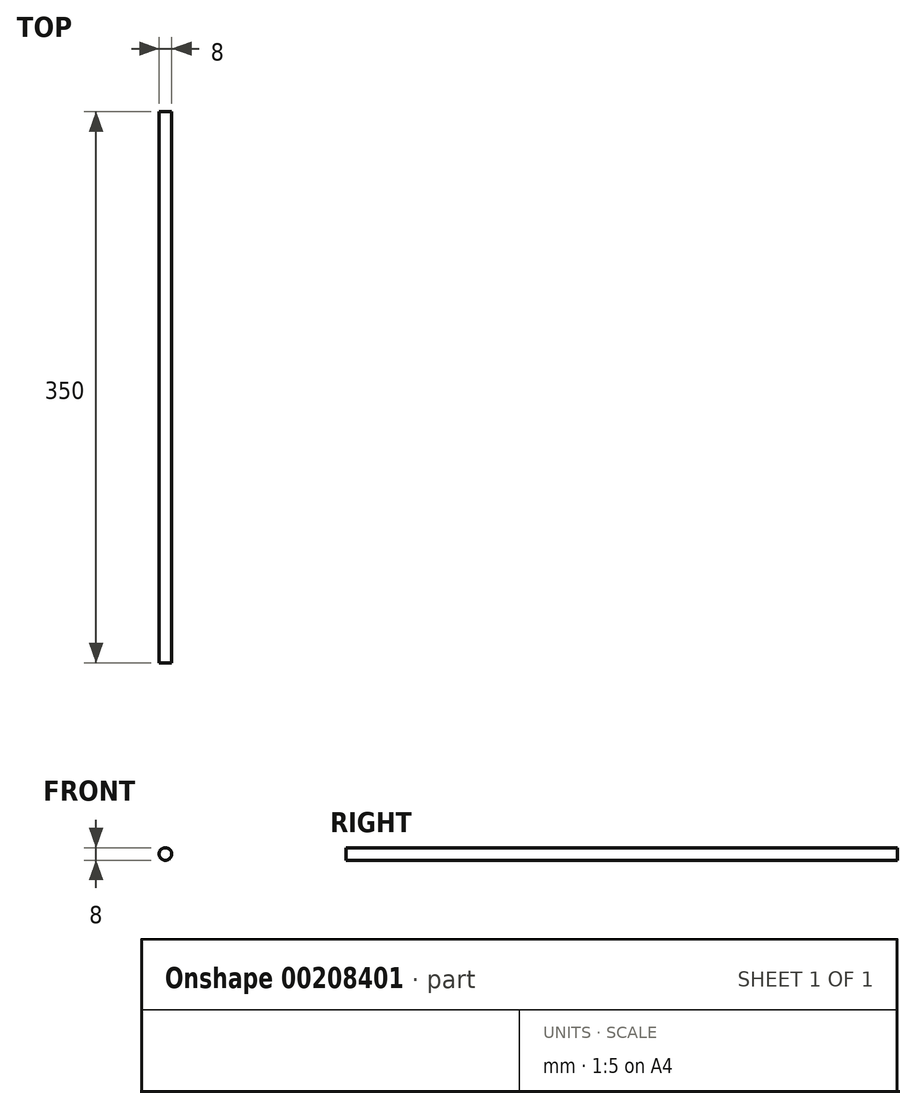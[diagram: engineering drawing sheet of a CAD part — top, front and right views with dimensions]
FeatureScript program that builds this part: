
annotation { "Feature Type Name" : "Feature", "Feature Type Description" : "" }
export const myFeature = defineFeature(function(context is Context, id is Id, definition is map)
    precondition{}
    {
        {
            var Q0;
            Q0=qCreatedBy(makeId("Front.planeOp"),FACE);
            var sketch = newSketch(context, id + "F0", { "sketchPlane" : qUnion([Q0])});
            skCircle(sketch, "E0", {"center": v(0, 0) * mm, "radius": 4 * mm});
            skSolve(sketch);
        }
        {
            var Q0;
            Q0 = qSketchRegion(id + "F0", true);
            extrude(context, id + "F1", {"entities" : qUnion([Q0]), "depth" : 350 * mm, "symmetric" : true});
        }
    });
